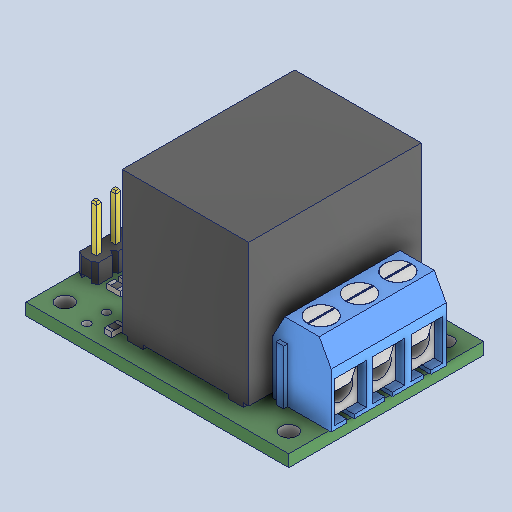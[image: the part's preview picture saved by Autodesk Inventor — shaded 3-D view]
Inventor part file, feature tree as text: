
AUTODESK INVENTOR PART (.ipt)
format: ipt  version: 2024 (Build 280153000, 153)  size: 1,817,088 bytes
history: native  units: in
note: dims shown in document units (in); Inventor stores cm internally (conversion verified against a paired STEP export)
features: other x4, projected_geometry x3, sketch x1
ambient origin geometry x8: Origin, YZ Plane, XZ Plane, XY Plane, X Axis, Y Axis, Z Axis, Center Point
bodies: Solid1 (feature_tree), Solid2 (feature_tree), Solid3 (feature_tree), Solid4 (feature_tree)
feature tree (8):
  sketch  "Sketch2"
  projected_geometry  "Projected Loop2"
  projected_geometry  "Projected Loop3"
  projected_geometry  "Projected Loop4"
  other  "relay"
  other  "header"
  other  "terminal block"
  other  "rcs03a"
